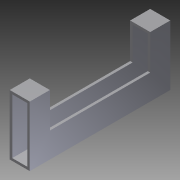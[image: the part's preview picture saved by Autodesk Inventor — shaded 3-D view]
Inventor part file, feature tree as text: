
AUTODESK INVENTOR PART (.ipt)
format: ipt  version: 2012 (Build 160160000, 160)  size: 95,744 bytes
history: native  units: in
note: dims shown in document units (in); Inventor stores cm internally (conversion verified against a paired STEP export)
features: extrude x2, sketch x2
ambient origin geometry x8: Origin, YZ Plane, XZ Plane, XY Plane, X Axis, Y Axis, Z Axis, Center Point
bodies: Solid1 (feature_tree)
feature tree (4):
  extrude  "Extrusion1"  Depth=1.0in
  extrude  "Extrusion2"  Depth=0.125in
  sketch  "Sketch1"  dims[d0=3.0in d1=1.0in]
  sketch  "Sketch2"  dims[d2=0.125in d3=0.125in d4=0.125in d5=0.125in d6=7.0in d7=0.0in d8=1.75in d9=1.0in d10=1.0in d11=7.0in d12=0.0in]
